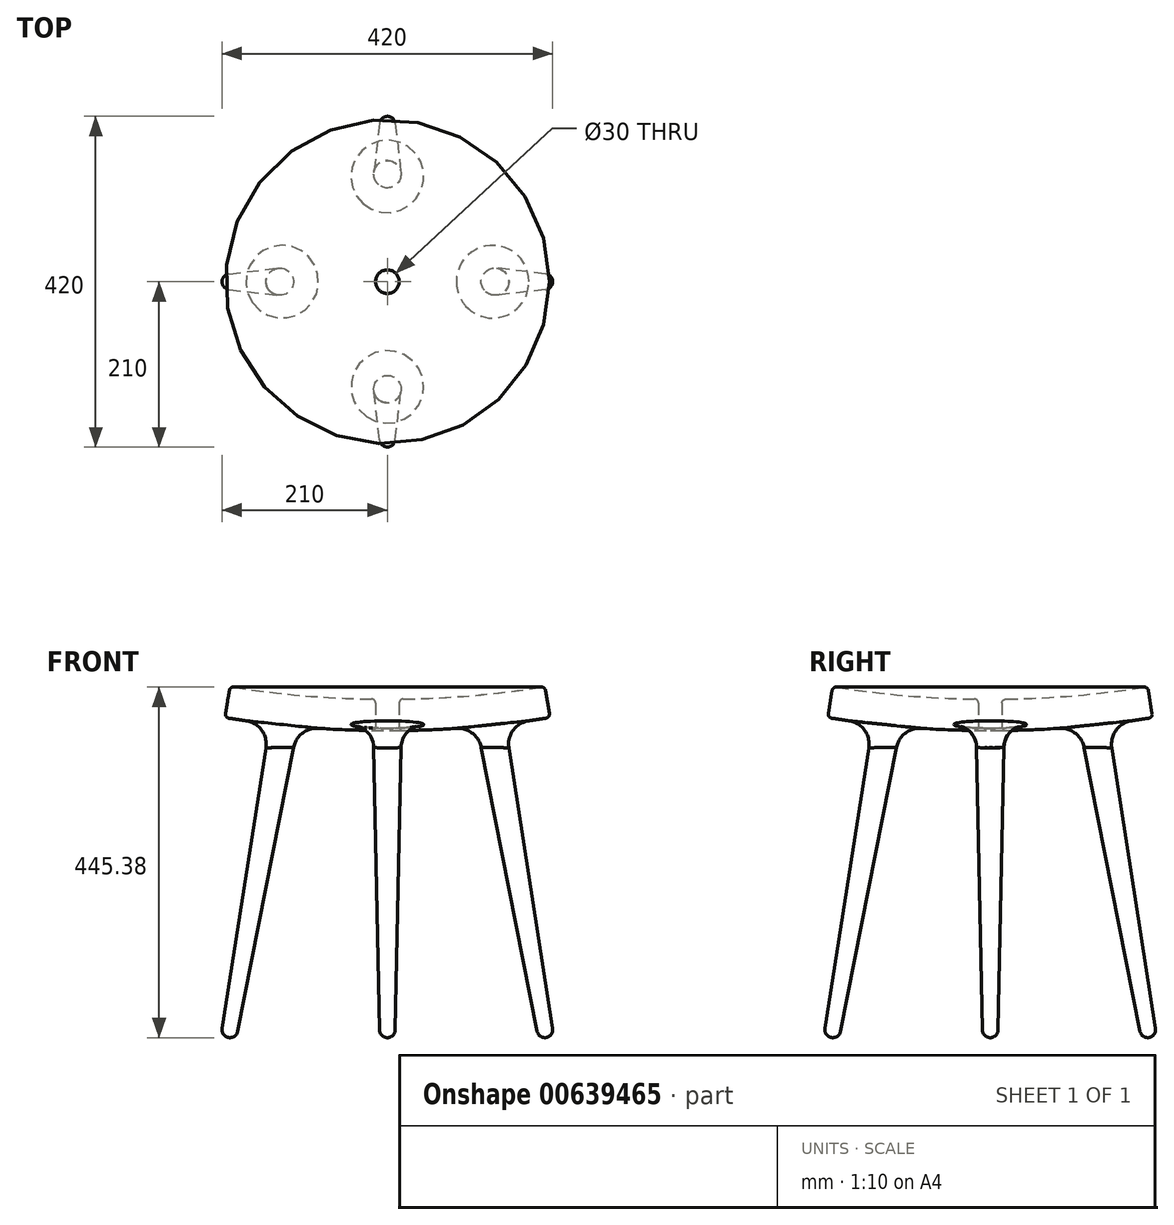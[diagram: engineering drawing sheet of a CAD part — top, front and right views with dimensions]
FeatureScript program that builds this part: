
annotation { "Feature Type Name" : "Feature", "Feature Type Description" : "" }
export const myFeature = defineFeature(function(context is Context, id is Id, definition is map)
    precondition{}
    {
        {
            var Q0;
            Q0=qCreatedBy(makeId("Front.planeOp"),FACE);
            var sketch = newSketch(context, id + "F0", { "sketchPlane" : qUnion([Q0])});
            skArc(sketch, "E0", {"start": v(0, 430) * mm, "mid": v(100.32, 434.03) * mm, "end": v(200, 446.1) * mm});
            skLineSegment(sketch, "E1", {"start": v(0, 1680) * mm, "end": v(0, 0) * mm});
            skLineSegment(sketch, "E2", {"start": v(200, 446.1) * mm, "end": v(206.4, 406.62) * mm});
            skArc(sketch, "E3.0", {"start": v(0, 390) * mm, "mid": v(103.53, 394.16) * mm, "end": v(206.4, 406.62) * mm});
            skLineSegment(sketch, "E4", {"start": v(0, 430) * mm, "end": v(0, 390) * mm});
            skSolve(sketch);
        }
        {
            var Q0;
            Q0=makeQuery(id+"F0.imprint","IMPRINT",FACE,{"disambiguationData":[TD([[makeQuery(id+"F0.imprint","IMPRINT",EDGE,{"derivedFrom":sQuery(id+"F0.wireOp",EDGE,"E0")}),-1.0]])]});
            var Q1;
            Q1=sQuery(id+"F0.wireOp",EDGE,"E4");
            revolve(context, id + "F1", {"entities" : qUnion([Q0]), "axis" : qUnion([Q1]), "revolveType" : RevolveType.FULL});
        }
        {
            var Q0;
            Q0=qCreatedBy(makeId("Front.planeOp"),FACE);
            var sketch = newSketch(context, id + "F2", { "sketchPlane" : qUnion([Q0])});
            skLineSegment(sketch, "E5", {"start": v(0, 0) * mm, "end": v(-374.66, 0) * mm});
            skArc(sketch, "E6", {"start": v(-201.74, 0.15) * mm, "mid": v(-194.35, 1.75) * mm, "end": v(-190.19, 8.07) * mm});
            skLineSegment(sketch, "E7", {"start": v(-201.76, 0) * mm, "end": v(-130.57, 403.77) * mm});
            skLineSegment(sketch, "E8", {"start": v(-130.57, 403.77) * mm, "end": v(-112.84, 400.65) * mm});
            skLineSegment(sketch, "E9", {"start": v(-112.84, 400.65) * mm, "end": v(-190.19, 8.07) * mm});
            skSolve(sketch);
        }
        {
            var Q0;
            {var subQ0=sQuery(id+"F2.wireOp",EDGE,"E8");Q0=makeQuery(id+"F2.imprint","IMPRINT",FACE,{"disambiguationData":[TD([[makeQuery(id+"F2.imprint","IMPRINT",EDGE,{"derivedFrom":subQ0}),-1.0]])]});}
            var Q1;
            Q1=sQuery(id+"F2.wireOp",EDGE,"E7");
            revolve(context, id + "F3", {"entities" : qUnion([Q0]), "axis" : qUnion([Q1]), "revolveType" : RevolveType.FULL});
        }
        {
            var Q0;
            Q0=qCreatedBy(makeId("Front.planeOp"),FACE);
            var sketch = newSketch(context, id + "F4", { "sketchPlane" : qUnion([Q0])});
            skLineSegment(sketch, "E10", {"start": v(0, 0) * mm, "end": v(0, 218.35) * mm});
            skSolve(sketch);
        }
        {
            var Q0;
            Q0=makeQuery(id+"F3.opRevolve","SWEPT_BODY",BODY,{"disambiguationData":[OSD([sQuery(id+"F2.wireOp",EDGE,"E6"),sQuery(id+"F2.wireOp",EDGE,"E7"),sQuery(id+"F2.wireOp",EDGE,"E8"),sQuery(id+"F2.wireOp",EDGE,"E9")])]});
            var Q1;
            Q1=sQuery(id+"F4.wireOp",EDGE,"E10");
            circularPattern(context, id + "F5", {"entities" : qUnion([Q0]), "axis" : qUnion([Q1]), "angle" : 360 * degree, "instanceCount" : 4, "equalSpace" : true});
        }
        {
            var Q0;
            Q0=makeQuery(id+"F1.opRevolve","SWEPT_BODY",BODY,{"disambiguationData":[OSD([sQuery(id+"F0.wireOp",EDGE,"E0"),sQuery(id+"F0.wireOp",EDGE,"E2"),sQuery(id+"F0.wireOp",EDGE,"E3.0"),sQuery(id+"F0.wireOp",EDGE,"E4")])]});
            var Q1;
            Q1=makeQuery(id+"F3.opRevolve","SWEPT_BODY",BODY,{"disambiguationData":[OSD([sQuery(id+"F2.wireOp",EDGE,"E6"),sQuery(id+"F2.wireOp",EDGE,"E7"),sQuery(id+"F2.wireOp",EDGE,"E8"),sQuery(id+"F2.wireOp",EDGE,"E9")])]});
            var Q2;
            Q2=makeQuery(id+"F5.opPattern","COPY",BODY,{"derivedFrom":makeQuery(id+"F3.opRevolve","SWEPT_BODY",BODY,{"disambiguationData":[OSD([sQuery(id+"F2.wireOp",EDGE,"E6"),sQuery(id+"F2.wireOp",EDGE,"E7"),sQuery(id+"F2.wireOp",EDGE,"E8"),sQuery(id+"F2.wireOp",EDGE,"E9")])]}),"instanceName":"2"});
            var Q3;
            Q3=makeQuery(id+"F5.opPattern","COPY",BODY,{"derivedFrom":makeQuery(id+"F3.opRevolve","SWEPT_BODY",BODY,{"disambiguationData":[OSD([sQuery(id+"F2.wireOp",EDGE,"E6"),sQuery(id+"F2.wireOp",EDGE,"E7"),sQuery(id+"F2.wireOp",EDGE,"E8"),sQuery(id+"F2.wireOp",EDGE,"E9")])]}),"instanceName":"3"});
            var Q4;
            Q4=makeQuery(id+"F5.opPattern","COPY",BODY,{"derivedFrom":makeQuery(id+"F3.opRevolve","SWEPT_BODY",BODY,{"disambiguationData":[OSD([sQuery(id+"F2.wireOp",EDGE,"E6"),sQuery(id+"F2.wireOp",EDGE,"E7"),sQuery(id+"F2.wireOp",EDGE,"E8"),sQuery(id+"F2.wireOp",EDGE,"E9")])]}),"instanceName":"1"});
            booleanBodies(context, id + "F6", {"operationType" : BooleanOperationType.UNION, "tools" : qUnion([Q0, Q1, Q2, Q3, Q4])});
        }
        {
            var Q0;
            Q0=makeQuery(id+"F6.opBoolean","INTERSECT",EDGE,{"derivedFrom":[makeQuery(id+"F1.opRevolve","SWEPT_FACE",FACE,{"disambiguationData":[OSD([sQuery(id+"F0.wireOp",EDGE,"E3.0")])]}),makeQuery(id+"F5.opPattern","COPY",FACE,{"derivedFrom":makeQuery(id+"F3.opRevolve","SWEPT_FACE",FACE,{"disambiguationData":[OSD([sQuery(id+"F2.wireOp",EDGE,"E9")])]}),"instanceName":"1"})]});
            var Q1;
            Q1=makeQuery(id+"F6.opBoolean","INTERSECT",EDGE,{"derivedFrom":[makeQuery(id+"F1.opRevolve","SWEPT_FACE",FACE,{"disambiguationData":[OSD([sQuery(id+"F0.wireOp",EDGE,"E3.0")])]}),makeQuery(id+"F5.opPattern","COPY",FACE,{"derivedFrom":makeQuery(id+"F3.opRevolve","SWEPT_FACE",FACE,{"disambiguationData":[OSD([sQuery(id+"F2.wireOp",EDGE,"E9")])]}),"instanceName":"2"})]});
            var Q2;
            Q2=makeQuery(id+"F6.opBoolean","INTERSECT",EDGE,{"derivedFrom":[makeQuery(id+"F1.opRevolve","SWEPT_FACE",FACE,{"disambiguationData":[OSD([sQuery(id+"F0.wireOp",EDGE,"E3.0")])]}),makeQuery(id+"F3.opRevolve","SWEPT_FACE",FACE,{"disambiguationData":[OSD([sQuery(id+"F2.wireOp",EDGE,"E9")])]})]});
            var Q3;
            Q3=makeQuery(id+"F6.opBoolean","INTERSECT",EDGE,{"derivedFrom":[makeQuery(id+"F1.opRevolve","SWEPT_FACE",FACE,{"disambiguationData":[OSD([sQuery(id+"F0.wireOp",EDGE,"E3.0")])]}),makeQuery(id+"F5.opPattern","COPY",FACE,{"derivedFrom":makeQuery(id+"F3.opRevolve","SWEPT_FACE",FACE,{"disambiguationData":[OSD([sQuery(id+"F2.wireOp",EDGE,"E9")])]}),"instanceName":"3"})]});
            fillet(context, id + "F7", {"entities" : qUnion([Q0, Q1, Q2, Q3]), "radius" : 30 * mm, "tangentPropagation" : true, "allowEdgeOverflow" : false});
        }
        {
            var Q0;
            Q0=makeQuery(id+"F1.opRevolve","SWEPT_EDGE",EDGE,{"disambiguationData":[OSD([sQuery(id+"F0.wireOp",EDGE,"E0"),sQuery(id+"F0.wireOp",EDGE,"E2")])]});
            var Q1;
            Q1=makeQuery(id+"F1.opRevolve","SWEPT_EDGE",EDGE,{"disambiguationData":[OSD([sQuery(id+"F0.wireOp",EDGE,"E2"),sQuery(id+"F0.wireOp",EDGE,"E3.0")])]});
            fillet(context, id + "F8", {"entities" : qUnion([Q0, Q1]), "radius" : 5 * mm, "tangentPropagation" : true, "allowEdgeOverflow" : false});
        }
        {
            var Q0;
            Q0=qCreatedBy(makeId("Top.planeOp"),FACE);
            var sketch = newSketch(context, id + "F9", { "sketchPlane" : qUnion([Q0])});
            skCircle(sketch, "E11", {"center": v(0, 0) * mm, "radius": 15 * mm});
            skSolve(sketch);
        }
        {
            var Q0;
            Q0=makeQuery(id+"F9.imprint","IMPRINT",FACE,{"disambiguationData":[TD([[makeQuery(id+"F9.imprint","IMPRINT",EDGE,{"derivedFrom":sQuery(id+"F9.wireOp",EDGE,"E11")}),1.0]])]});
            var Q1;
            Q1=sQuery(id+"F9.wireOp",EDGE,"E11");
            extrude(context, id + "F10", {"entities" : qUnion([Q0]), "operationType" : NewBodyOperationType.REMOVE, "surfaceEntities" : qUnion([Q1]), "depth" : 656 * mm, "offsetDistance" : 25 * mm});
        }
        {
            var Q0;
            Q0=makeQuery(id+"F10.boolean.opBoolean","INTERSECT",EDGE,{"derivedFrom":[makeQuery(id+"F1.opRevolve","SWEPT_FACE",FACE,{"disambiguationData":[OSD([sQuery(id+"F0.wireOp",EDGE,"E3.0")])]}),makeQuery(id+"F10.opExtrude","SWEPT_FACE",FACE,{"disambiguationData":[OSD([sQuery(id+"F9.wireOp",EDGE,"E11")])]})]});
            var Q1;
            Q1=makeQuery(id+"F10.boolean.opBoolean","INTERSECT",EDGE,{"derivedFrom":[makeQuery(id+"F1.opRevolve","SWEPT_FACE",FACE,{"disambiguationData":[OSD([sQuery(id+"F0.wireOp",EDGE,"E0")])]}),makeQuery(id+"F10.opExtrude","SWEPT_FACE",FACE,{"disambiguationData":[OSD([sQuery(id+"F9.wireOp",EDGE,"E11")])]})]});
            fillet(context, id + "F11", {"entities" : qUnion([Q0, Q1]), "radius" : 5 * mm, "tangentPropagation" : true, "allowEdgeOverflow" : false});
        }
    });
